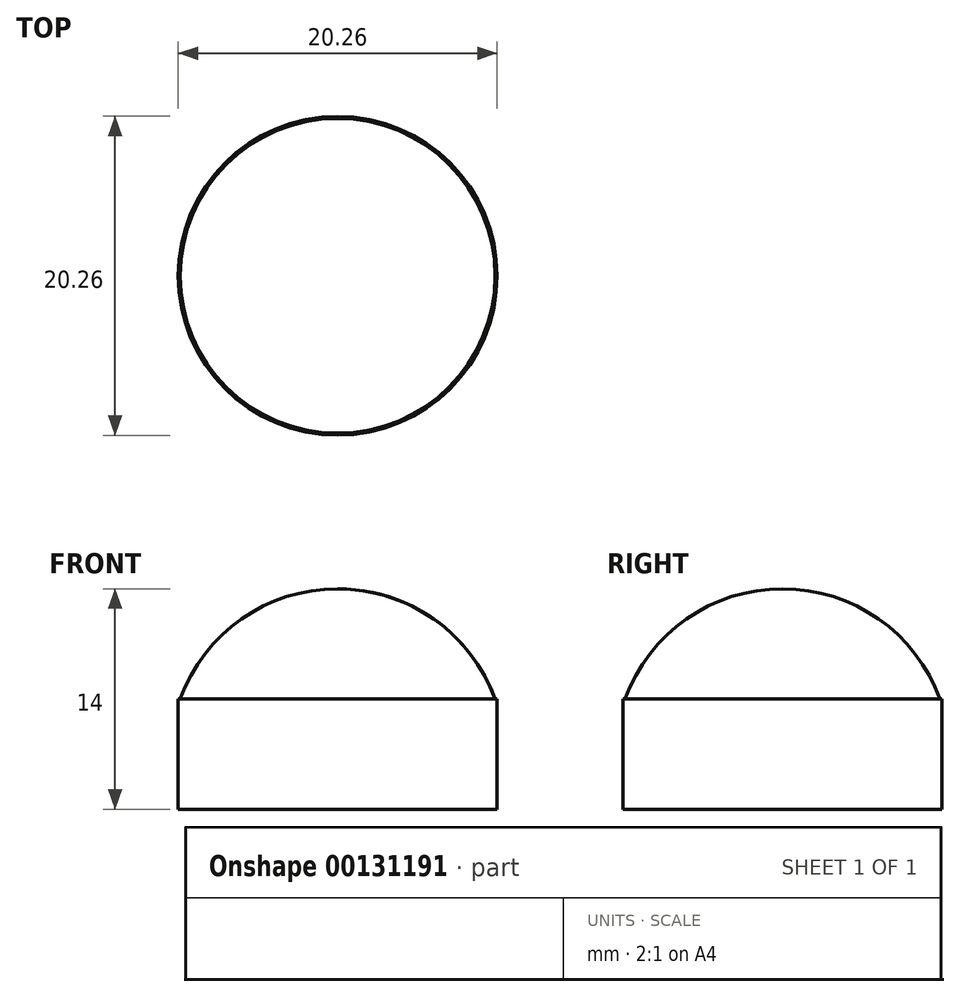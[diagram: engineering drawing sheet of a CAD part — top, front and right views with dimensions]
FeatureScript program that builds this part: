
annotation { "Feature Type Name" : "Feature", "Feature Type Description" : "" }
export const myFeature = defineFeature(function(context is Context, id is Id, definition is map)
    precondition{}
    {
        {
            var Q0;
            Q0=qCreatedBy(makeId("Top.planeOp"),FACE);
            var sketch = newSketch(context, id + "F0", { "sketchPlane" : qUnion([Q0])});
            skCircle(sketch, "E0", {"center": v(0, 0) * mm, "radius": 10.12 * mm});
            skSolve(sketch);
        }
        {
            var Q0;
            Q0=qSketchRegion(id+"F0",true);
            extrude(context, id + "F1", {"entities" : qUnion([Q0]), "depth" : 7 * mm});
        }
        {
            var Q0;
            Q0=qCreatedBy(makeId("Front.planeOp"),FACE);
            var sketch = newSketch(context, id + "F2", { "sketchPlane" : qUnion([Q0])});
            skArc(sketch, "E1", {"start": v(0, 14) * mm, "mid": v(-6.1, 12.08) * mm, "end": v(-10, 7) * mm});
            skLineSegment(sketch, "E2", {"start": v(-10, 7) * mm, "end": v(0, 7) * mm});
            skLineSegment(sketch, "E3", {"start": v(0, 14) * mm, "end": v(0, 7) * mm});
            skSolve(sketch);
        }
        {
            var Q0;
            Q0=qSketchRegion(id+"F2",true);
            var Q1;
            Q1=sQuery(id+"F2.wireOp",EDGE,"E3");
            revolve(context, id + "F3", {"operationType" : NewBodyOperationType.ADD, "entities" : qUnion([Q0]), "axis" : qUnion([Q1]), "revolveType" : RevolveType.FULL});
        }
    });
